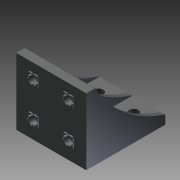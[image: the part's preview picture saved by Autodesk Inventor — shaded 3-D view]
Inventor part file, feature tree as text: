
AUTODESK INVENTOR PART (.ipt)
format: ipt  version: 2011 SP1 (Build 150282100, 282)  size: 349,696 bytes
history: native  units: mm
features: other x132, extrude x16, sketch x10
ambient origin geometry x8: Origin, YZ Plane, XZ Plane, XY Plane, X Axis, Y Axis, Z Axis, Center Point
bodies: Solid1 (feature_tree)
feature tree (158):
  extrude  "Extrusion1"  Depth=35.0mm TaperAngle=0.0deg
  extrude  "Extrusion2"  Depth=40.0mm TaperAngle=0.0deg
  extrude  "Extrusion3"  Depth=5.0mm TaperAngle=0.0deg
  extrude  "Extrusion4"  Depth=5.0mm TaperAngle=0.0deg
  extrude  "Extrusion5"  Depth=5.0mm TaperAngle=0.0deg
  other  "Pattern_3_SKETCH_1"
  other  "Pattern_3_SKETCH_2"
  other  "Pattern_3_SKETCH_3"
  extrude  "Extrusion6"  Depth=5.0mm TaperAngle=0.0deg
  extrude  "Extrusion7"  Depth=0.8mm TaperAngle=0.0deg
  extrude  "Extrusion8"  Depth=1.25mm TaperAngle=0.0deg
  extrude  "Extrusion9"  [1 undecoded]
  other  "Pattern_4_SKETCH_1"
  other  "Pattern_4_SKETCH_2"
  other  "Pattern_4_SKETCH_3"
  extrude  "Extrusion10"  [1 undecoded]
  extrude  "Extrusion11"  [1 undecoded]
  extrude  "Extrusion12"  [1 undecoded]
  extrude  "Extrusion13"  [1 undecoded]
  extrude  "Extrusion14"  [1 undecoded]
  extrude  "Extrusion15"  [1 undecoded]
  extrude  "Extrusion16"  [1 undecoded]
  other  "4_bolt_row_12_1_XY"
  other  "4_bolt_row_12_1_YZ"
  other  "4_bolt_row_12_1_ZX"
  other  "4_bolt_row_12_1_X"
  other  "4_bolt_row_12_1_Y"
  other  "4_bolt_row_12_1_Z"
  other  "4_bolt_row_12_1_Center"
  other  "4_bolt_row_12_2_XY"
  other  "4_bolt_row_12_2_YZ"
  other  "4_bolt_row_12_2_ZX"
  other  "4_bolt_row_12_2_X"
  other  "4_bolt_row_12_2_Y"
  other  "4_bolt_row_12_2_Z"
  other  "4_bolt_row_12_2_Center"
  other  "4_bolt_row_12_3_XY"
  other  "4_bolt_row_12_3_YZ"
  other  "4_bolt_row_12_3_ZX"
  other  "4_bolt_row_12_3_X"
  other  "4_bolt_row_12_3_Y"
  other  "4_bolt_row_12_3_Z"
  other  "4_bolt_row_12_3_Center"
  other  "4_bolt_row_12_4_XY"
  other  "4_bolt_row_12_4_YZ"
  other  "4_bolt_row_12_4_ZX"
  other  "4_bolt_row_12_4_X"
  other  "4_bolt_row_12_4_Y"
  other  "4_bolt_row_12_4_Z"
  other  "4_bolt_row_12_4_Center"
  other  "4_hole_row_12_base_1_XY"
  other  "4_hole_row_12_base_1_YZ"
  other  "4_hole_row_12_base_1_ZX"
  other  "4_hole_row_12_base_1_X"
  other  "4_hole_row_12_base_1_Y"
  other  "4_hole_row_12_base_1_Z"
  other  "4_hole_row_12_base_1_Center"
  other  "4_hole_row_12_base_2_XY"
  other  "4_hole_row_12_base_2_YZ"
  other  "4_hole_row_12_base_2_ZX"
  other  "4_hole_row_12_base_2_X"
  other  "4_hole_row_12_base_2_Y"
  other  "4_hole_row_12_base_2_Z"
  other  "4_hole_row_12_base_2_Center"
  other  "4_hole_row_12_base_3_XY"
  other  "4_hole_row_12_base_3_YZ"
  other  "4_hole_row_12_base_3_ZX"
  other  "4_hole_row_12_base_3_X"
  other  "4_hole_row_12_base_3_Y"
  other  "4_hole_row_12_base_3_Z"
  other  "4_hole_row_12_base_3_Center"
  other  "4_hole_row_12_base_4_XY"
  other  "4_hole_row_12_base_4_YZ"
  other  "4_hole_row_12_base_4_ZX"
  other  "4_hole_row_12_base_4_X"
  other  "4_hole_row_12_base_4_Y"
  other  "4_hole_row_12_base_4_Z"
  other  "4_hole_row_12_base_4_Center"
  other  "4_nut_row_12_1_XY"
  other  "4_nut_row_12_1_YZ"
  other  "4_nut_row_12_1_ZX"
  other  "4_nut_row_12_1_X"
  other  "4_nut_row_12_1_Y"
  other  "4_nut_row_12_1_Z"
  other  "4_nut_row_12_1_Center"
  other  "4_nut_row_12_2_XY"
  other  "4_nut_row_12_2_YZ"
  other  "4_nut_row_12_2_ZX"
  other  "4_nut_row_12_2_X"
  other  "4_nut_row_12_2_Y"
  other  "4_nut_row_12_2_Z"
  other  "4_nut_row_12_2_Center"
  other  "4_nut_row_12_3_XY"
  other  "4_nut_row_12_3_YZ"
  other  "4_nut_row_12_3_ZX"
  other  "4_nut_row_12_3_X"
  other  "4_nut_row_12_3_Y"
  other  "4_nut_row_12_3_Z"
  other  "4_nut_row_12_3_Center"
  other  "4_nut_row_12_4_XY"
  other  "4_nut_row_12_4_YZ"
  other  "4_nut_row_12_4_ZX"
  other  "4_nut_row_12_4_X"
  other  "4_nut_row_12_4_Y"
  other  "4_nut_row_12_4_Z"
  other  "4_nut_row_12_4_Center"
  other  "4_nut_row_12_base_1_XY"
  other  "4_nut_row_12_base_1_YZ"
  other  "4_nut_row_12_base_1_ZX"
  other  "4_nut_row_12_base_1_X"
  other  "4_nut_row_12_base_1_Y"
  other  "4_nut_row_12_base_1_Z"
  other  "4_nut_row_12_base_1_Center"
  other  "4_nut_row_12_base_2_XY"
  other  "4_nut_row_12_base_2_YZ"
  other  "4_nut_row_12_base_2_ZX"
  other  "4_nut_row_12_base_2_X"
  other  "4_nut_row_12_base_2_Y"
  other  "4_nut_row_12_base_2_Z"
  other  "4_nut_row_12_base_2_Center"
  other  "4_nut_row_12_base_3_XY"
  other  "4_nut_row_12_base_3_YZ"
  other  "4_nut_row_12_base_3_ZX"
  other  "4_nut_row_12_base_3_X"
  other  "4_nut_row_12_base_3_Y"
  other  "4_nut_row_12_base_3_Z"
  other  "4_nut_row_12_base_3_Center"
  other  "4_nut_row_12_base_4_XY"
  other  "4_nut_row_12_base_4_YZ"
  other  "4_nut_row_12_base_4_ZX"
  other  "4_nut_row_12_base_4_X"
  other  "4_nut_row_12_base_4_Y"
  other  "4_nut_row_12_base_4_Z"
  other  "4_nut_row_12_base_4_Center"
  other  "bracket_to_bolt_XY"
  other  "bracket_to_bolt_YZ"
  other  "bracket_to_bolt_ZX"
  other  "bracket_to_bolt_X"
  other  "bracket_to_bolt_Y"
  other  "bracket_to_bolt_Z"
  other  "bracket_to_bolt_Center"
  other  "bracket_to_dummy_XY"
  other  "bracket_to_dummy_YZ"
  other  "bracket_to_dummy_ZX"
  other  "bracket_to_dummy_X"
  other  "bracket_to_dummy_Y"
  other  "bracket_to_dummy_Z"
  other  "bracket_to_dummy_Center"
  sketch  "Sketch_15"  dims[d20=5.0mm d21=0.0mm d22=5.0mm d23=0.0mm]
  sketch  "Sketch_16"  dims[d24=0.8mm d25=0.0mm d26=0.8mm d27=0.0mm]
  sketch  "Sketch_21"  dims[d28=0.8mm d29=0.0mm d30=1.25mm d31=0.0mm]
  sketch  "Sketch_28"
  sketch  "Sketch_22_ALT_Drilling_1"  dims[d0=40.0mm d1=0.0mm d2=35.0mm d3=0.0mm]
  sketch  "Sketch_24_ALT_Drilling_2"  dims[d8=5.0mm d9=0.0mm d10=5.0mm d11=0.0mm]
  sketch  "Sketch_1"  dims[d4=2.5mm d5=0.0mm d6=40.0mm d7=0.0mm]
  sketch  "Sketch_10"  dims[d12=5.0mm d13=0.0mm d14=5.0mm d15=0.0mm]
  sketch  "Sketch_14"  dims[d16=5.0mm d17=0.0mm d18=5.0mm d19=0.0mm]
  sketch  "Sketch_27"  dims[d32=0.0mm d33=0.0mm d34=0.0mm d35=0.0mm d36=0.0mm d37=0.0mm d38=0.0mm d39=0.0mm]
note: 8 required parameter values undecoded (feature->parameter linkage not recoverable at this tier; creation-order binding heuristic only, values carry confidence <= 0.55)
